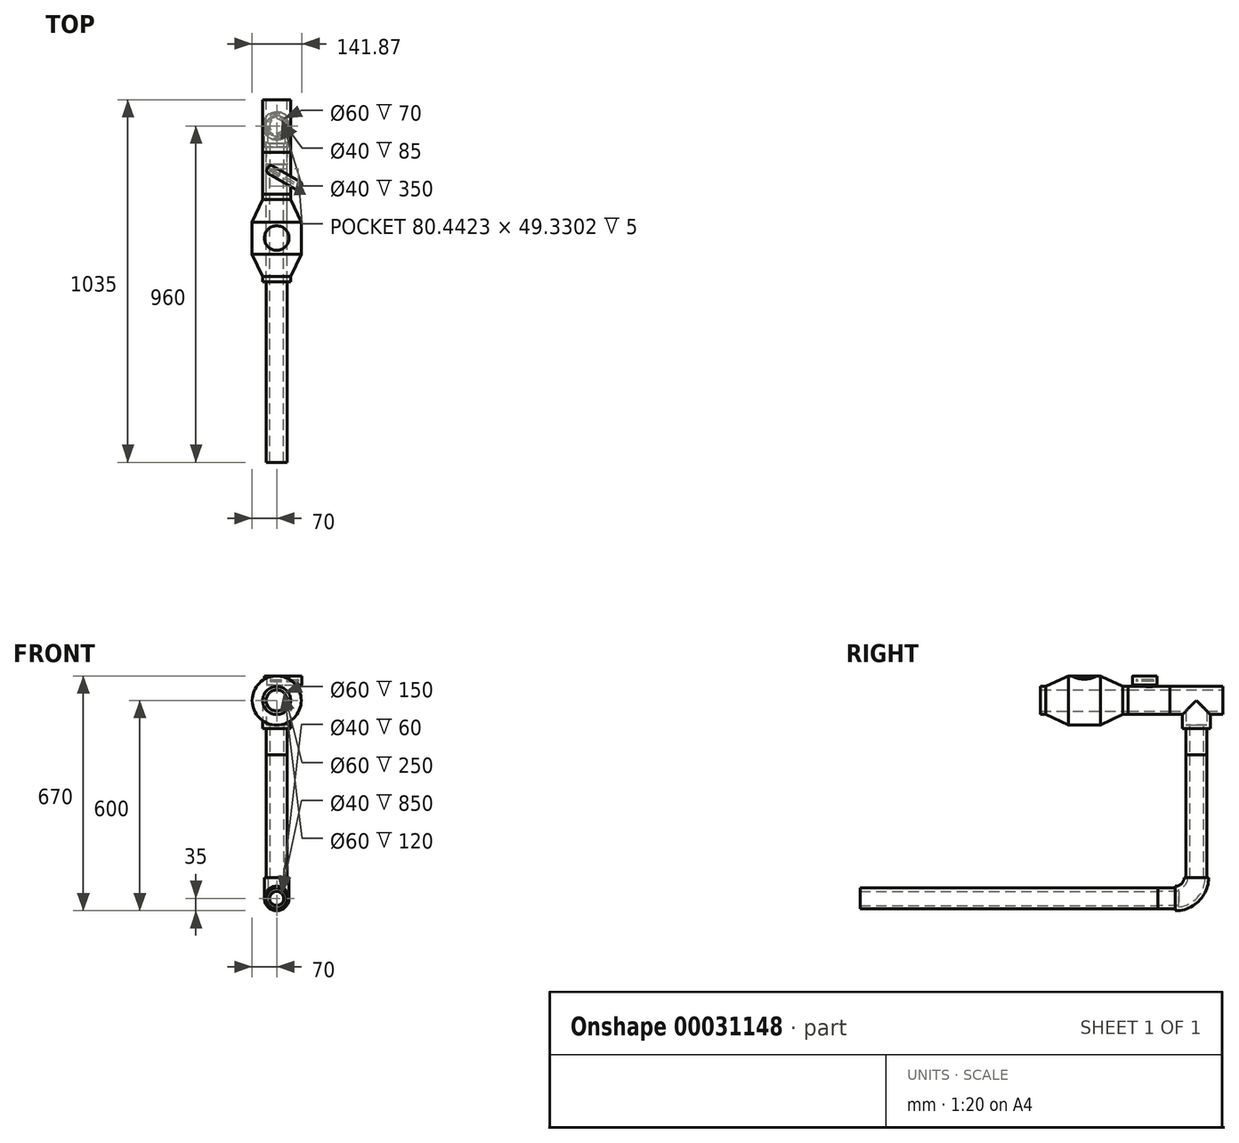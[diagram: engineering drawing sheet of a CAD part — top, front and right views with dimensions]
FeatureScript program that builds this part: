
annotation { "Feature Type Name" : "Feature", "Feature Type Description" : "" }
export const myFeature = defineFeature(function(context is Context, id is Id, definition is map)
    precondition{}
    {
        {
            var Q0;
            Q0=qCreatedBy(makeId("Front.planeOp"),FACE);
            var sketch = newSketch(context, id + "F0", { "sketchPlane" : qUnion([Q0])});
            skCircle(sketch, "E0", {"center": v(0, 0) * mm, "radius": 30 * mm});
            skSolve(sketch);
        }
        {
            var Q0;
            Q0 = qSketchRegion(id + "F0", true);
            extrude(context, id + "F1", {"entities" : qUnion([Q0]), "depth" : 850 * mm});
        }
        {
            var Q0;
            Q0=makeQuery(id+"F1.opExtrude","CAP_FACE",FACE,{"disambiguationData":[OSD([sQuery(id+"F0.wireOp",EDGE,"E0")])],"isStart":true});
            var sketch = newSketch(context, id + "F2", { "sketchPlane" : qUnion([Q0])});
            skCircle(sketch, "E1.0", {"center": v(0, 0) * mm, "radius": 30 * mm});
            skSolve(sketch);
        }
        {
            var Q0;
            Q0 = qSketchRegion(id + "F2", true);
            extrude(context, id + "F3", {"entities" : qUnion([Q0]), "depth" : 50 * mm});
        }
        {
            var Q0;
            Q0=qCreatedBy(makeId("Right.planeOp"),FACE);
            var sketch = newSketch(context, id + "F4", { "sketchPlane" : qUnion([Q0])});
            skArc(sketch, "E2", {"start": v(50, 0) * mm, "mid": v(92.43, 17.57) * mm, "end": v(110, 60) * mm});
            skLineSegment(sketch, "E3", {"start": v(50, 0) * mm, "end": v(-58.8, 0) * mm, "construction": true});
            skLineSegment(sketch, "E4", {"start": v(110, 60) * mm, "end": v(110, 125.75) * mm, "construction": true});
            skSolve(sketch);
        }
        {
            var Q0;
            Q0=makeQuery(id+"F3.opExtrude","CAP_FACE",FACE,{"disambiguationData":[OSD([sQuery(id+"F2.wireOp",EDGE,"E1.0")])],"isStart":false});
            var sketch = newSketch(context, id + "F5", { "sketchPlane" : qUnion([Q0])});
            skCircle(sketch, "E5", {"center": v(0, 0) * mm, "radius": 35 * mm});
            skSolve(sketch);
        }
        {
            var Q0;
            Q0 = qSketchRegion(id + "F5", true);
            var Q1;
            Q1 = qConstructionFilter(qBodyType(qCreatedBy(id + "F4" ,EDGE), BodyType.WIRE), ConstructionObject.NO);
            sweep(context, id + "F6", {"operationType" : NewBodyOperationType.ADD, "profiles" : qUnion([Q0]), "path" : qUnion([Q1])});
        }
        {
            var Q0;
            Q0=makeQuery(id+"F6.opSweep","CAP_FACE",FACE,{"disambiguationData":[OSD([sQuery(id+"F4.wireOp",VERTEX,"E2.end"),sQuery(id+"F5.wireOp",EDGE,"E5")])],"isStart":false});
            var sketch = newSketch(context, id + "F7", { "sketchPlane" : qUnion([Q0])});
            skCircle(sketch, "E6", {"center": v(0, 110) * mm, "radius": 30 * mm});
            skPoint(sketch, "E7", {"position": v(0, 140) * mm});
            skSolve(sketch);
        }
        {
            var Q0;
            Q0 = qSketchRegion(id + "F7", true);
            extrude(context, id + "F8", {"entities" : qUnion([Q0]), "depth" : 350 * mm});
        }
        {
            var Q0;
            Q0=makeQuery(id+"F8.opExtrude","CAP_FACE",FACE,{"disambiguationData":[OSD([sQuery(id+"F7.wireOp",EDGE,"E6")])],"isStart":false});
            var sketch = newSketch(context, id + "F9", { "sketchPlane" : qUnion([Q0])});
            skCircle(sketch, "E8.0", {"center": v(0, 110) * mm, "radius": 30 * mm});
            skSolve(sketch);
        }
        {
            var Q0;
            Q0 = qSketchRegion(id + "F9", true);
            extrude(context, id + "F10", {"entities" : qUnion([Q0]), "depth" : 75 * mm});
        }
        {
            var Q0;
            Q0=makeQuery(id+"F10.opExtrude","CAP_FACE",FACE,{"disambiguationData":[OSD([sQuery(id+"F9.wireOp",EDGE,"E8.0")])],"isStart":false});
            var sketch = newSketch(context, id + "F11", { "sketchPlane" : qUnion([Q0])});
            skCircle(sketch, "E9", {"center": v(0, 110) * mm, "radius": 40 * mm});
            skSolve(sketch);
        }
        {
            var Q0;
            Q0 = qSketchRegion(id + "F11", true);
            extrude(context, id + "F12", {"entities" : qUnion([Q0]), "operationType" : NewBodyOperationType.ADD, "depth" : 80 * mm});
        }
        {
            var Q0;
            Q0=sQuery(id+"F11.wireOp",VERTEX,"E9.center");
            var Q1;
            Q1=qCreatedBy(makeId("Front.planeOp"),FACE);
            cPlane(context, id + "F13", {"entities" : qUnion([Q0, Q1]), "cplaneType" : CPlaneType.PLANE_POINT, "offset" : 150 * mm, "width" : 150 * mm, "height" : 150 * mm});
        }
        {
            var Q0;
            Q0=qCreatedBy(id+"F13.planeOp",FACE);
            var sketch = newSketch(context, id + "F14", { "sketchPlane" : qUnion([Q0])});
            skCircle(sketch, "E10", {"center": v(0, 565) * mm, "radius": 40 * mm});
            skSolve(sketch);
        }
        {
            var Q0;
            Q0 = qSketchRegion(id + "F14", true);
            extrude(context, id + "F15", {"entities" : qUnion([Q0]), "operationType" : NewBodyOperationType.ADD, "depth" : 150 * mm, "symmetric" : true});
        }
        {
            var Q0;
            Q0=makeQuery(id+"F15.opExtrude","CAP_FACE",FACE,{"disambiguationData":[OSD([sQuery(id+"F14.wireOp",EDGE,"E10")])],"isStart":false});
            var sketch = newSketch(context, id + "F16", { "sketchPlane" : qUnion([Q0])});
            skCircle(sketch, "E11.0", {"center": v(0, 565) * mm, "radius": 40 * mm});
            skSolve(sketch);
        }
        {
            var Q0;
            Q0 = qSketchRegion(id + "F16", true);
            extrude(context, id + "F17", {"entities" : qUnion([Q0]), "depth" : 120 * mm});
        }
        {
            var Q0;
            Q0=qCreatedBy(makeId("Right.planeOp"),FACE);
            var sketch = newSketch(context, id + "F18", { "sketchPlane" : qUnion([Q0])});
            skLineSegment(sketch, "E12", {"start": v(-25, 565) * mm, "end": v(-25, 610) * mm});
            skLineSegment(sketch, "E13", {"start": v(-25, 565) * mm, "end": v(-35, 565) * mm});
            skLineSegment(sketch, "E14", {"start": v(-35, 565) * mm, "end": v(-35, 610) * mm});
            skLineSegment(sketch, "E15", {"start": v(-35, 610) * mm, "end": v(-25, 610) * mm});
            skSolve(sketch);
        }
        {
            var Q0;
            Q0 = qSketchRegion(id + "F18", true);
            var Q1;
            Q1=sQuery(id+"F18.wireOp",EDGE,"E12");
            revolve(context, id + "F19", {"operationType" : NewBodyOperationType.ADD, "entities" : qUnion([Q0]), "axis" : qUnion([Q1]), "revolveType" : RevolveType.FULL});
        }
        {
            var Q0;
            Q0=makeQuery(id+"F19.opRevolve","SWEPT_FACE",FACE,{"disambiguationData":[OSD([sQuery(id+"F18.wireOp",EDGE,"E15")])]});
            var sketch = newSketch(context, id + "F20", { "sketchPlane" : qUnion([Q0])});
            skLineSegment(sketch, "E16.bottom", {"start": v(-11.07, -4.17) * mm, "end": v(66.87, -49.17) * mm});
            skLineSegment(sketch, "E16.top", {"start": v(-23.57, -25.83) * mm, "end": v(54.37, -70.83) * mm});
            skLineSegment(sketch, "E16.left", {"start": v(-24.73, -7.83) * mm, "end": v(-27.23, -12.17) * mm});
            skLineSegment(sketch, "E16.right", {"start": v(70.53, -62.83) * mm, "end": v(68.03, -67.17) * mm});
            skLineSegment(sketch, "E17", {"start": v(-25.98, -10) * mm, "end": v(69.28, -65) * mm, "construction": true});
            skPoint(sketch, "E18", {"position": v(0, -25) * mm});
            skPoint(sketch, "E19.visualSharp", {"position": v(-19.73, 0.83) * mm});
            skArc(sketch, "E19.filletArc", {"start": v(-11.07, -4.17) * mm, "mid": v(-18.66, -3.18) * mm, "end": v(-24.73, -7.83) * mm});
            skPoint(sketch, "E20.visualSharp", {"position": v(75.53, -54.17) * mm});
            skArc(sketch, "E20.filletArc", {"start": v(70.53, -62.83) * mm, "mid": v(71.53, -55.25) * mm, "end": v(66.87, -49.17) * mm});
            skPoint(sketch, "E21.visualSharp", {"position": v(63.03, -75.83) * mm});
            skArc(sketch, "E21.filletArc", {"start": v(54.37, -70.83) * mm, "mid": v(61.96, -71.82) * mm, "end": v(68.03, -67.17) * mm});
            skPoint(sketch, "E22.visualSharp", {"position": v(-32.23, -20.83) * mm});
            skArc(sketch, "E22.filletArc", {"start": v(-27.23, -12.17) * mm, "mid": v(-28.23, -19.75) * mm, "end": v(-23.57, -25.83) * mm});
            skLineSegment(sketch, "E23", {"start": v(0, -25) * mm, "end": v(80.42, -25) * mm, "construction": true});
            skSolve(sketch);
        }
        {
            var Q0;
            Q0 = qSketchRegion(id + "F20", true);
            extrude(context, id + "F21", {"entities" : qUnion([Q0]), "operationType" : NewBodyOperationType.ADD, "depth" : 25 * mm});
        }
        {
            var Q0;
            Q0=makeQuery(id+"F17.opExtrude","CAP_FACE",FACE,{"disambiguationData":[OSD([sQuery(id+"F16.wireOp",EDGE,"E11.0")])],"isStart":false});
            var sketch = newSketch(context, id + "F22", { "sketchPlane" : qUnion([Q0])});
            skCircle(sketch, "E24.0", {"center": v(0, 565) * mm, "radius": 40 * mm});
            skSolve(sketch);
        }
        {
            var Q0;
            Q0 = qSketchRegion(id + "F22", true);
            extrude(context, id + "F23", {"entities" : qUnion([Q0]), "depth" : 250 * mm});
        }
        {
            var Q0;
            Q0=makeQuery(id+"F17.opExtrude","CAP_FACE",FACE,{"disambiguationData":[OSD([sQuery(id+"F16.wireOp",EDGE,"E11.0")])],"isStart":false});
            var Q1;
            Q1=makeQuery(id+"F15.opExtrude","CAP_FACE",FACE,{"disambiguationData":[OSD([sQuery(id+"F14.wireOp",EDGE,"E10")])],"isStart":true});
            var Q2;
            Q2=makeQuery(id+"F1.opExtrude","CAP_FACE",FACE,{"disambiguationData":[OSD([sQuery(id+"F0.wireOp",EDGE,"E0")])],"isStart":false});
            var Q3;
            Q3=makeQuery(id+"F3.opExtrude","CAP_FACE",FACE,{"disambiguationData":[OSD([sQuery(id+"F2.wireOp",EDGE,"E1.0")])],"isStart":true});
            var Q4;
            Q4=makeQuery(id+"F6.opSweep","CAP_FACE",FACE,{"disambiguationData":[OSD([sQuery(id+"F4.wireOp",VERTEX,"E2.end"),sQuery(id+"F5.wireOp",EDGE,"E5")])],"isStart":false});
            var Q5;
            Q5=makeQuery(id+"F10.opExtrude","CAP_FACE",FACE,{"disambiguationData":[OSD([sQuery(id+"F9.wireOp",EDGE,"E8.0")])],"isStart":true});
            var Q6;
            Q6=makeQuery(id+"F15.opExtrude","CAP_FACE",FACE,{"disambiguationData":[OSD([sQuery(id+"F14.wireOp",EDGE,"E10")])],"isStart":false});
            var Q7;
            Q7=makeQuery(id+"F8.opExtrude","CAP_FACE",FACE,{"disambiguationData":[OSD([sQuery(id+"F7.wireOp",EDGE,"E6")])],"isStart":false});
            var Q8;
            Q8=makeQuery(id+"F17.opExtrude","CAP_FACE",FACE,{"disambiguationData":[OSD([sQuery(id+"F16.wireOp",EDGE,"E11.0")])],"isStart":true});
            var Q9;
            Q9=makeQuery(id+"F8.opExtrude","CAP_FACE",FACE,{"disambiguationData":[OSD([sQuery(id+"F7.wireOp",EDGE,"E6")])],"isStart":true});
            var Q10;
            Q10=makeQuery(id+"F1.opExtrude","CAP_FACE",FACE,{"disambiguationData":[OSD([sQuery(id+"F0.wireOp",EDGE,"E0")])],"isStart":true});
            var Q11;
            Q11=makeQuery(id+"F23.opExtrude","CAP_FACE",FACE,{"disambiguationData":[OSD([sQuery(id+"F22.wireOp",EDGE,"E24.0")])],"isStart":false});
            var Q12;
            Q12=makeQuery(id+"F23.opExtrude","CAP_FACE",FACE,{"disambiguationData":[OSD([sQuery(id+"F22.wireOp",EDGE,"E24.0")])],"isStart":true});
            var Q13;
            Q13=makeQuery(id+"F17.opExtrude","SWEPT_BODY",BODY,{"disambiguationData":[OSD([sQuery(id+"F16.wireOp",EDGE,"E11.0")])]});
            var Q14;
            Q14=makeQuery(id+"F8.opExtrude","SWEPT_BODY",BODY,{"disambiguationData":[OSD([sQuery(id+"F7.wireOp",EDGE,"E6")])]});
            var Q15;
            Q15=makeQuery(id+"F10.opExtrude","SWEPT_BODY",BODY,{"disambiguationData":[OSD([sQuery(id+"F9.wireOp",EDGE,"E8.0")])]});
            var Q16;
            Q16=makeQuery(id+"F3.opExtrude","SWEPT_BODY",BODY,{"disambiguationData":[OSD([sQuery(id+"F2.wireOp",EDGE,"E1.0")])]});
            var Q17;
            Q17=makeQuery(id+"F1.opExtrude","SWEPT_BODY",BODY,{"disambiguationData":[OSD([sQuery(id+"F0.wireOp",EDGE,"E0")])]});
            shell(context, id + "F24", {"entities" : qUnion([Q0, Q1, Q2, Q3, Q4, Q5, Q6, Q7, Q8, Q9, Q10, Q11, Q12]), "parts" : qUnion([Q13, Q14, Q15, Q16, Q17]), "thickness" : 10 * mm});
        }
        {
            var Q0;
            Q0=qCreatedBy(makeId("Right.planeOp"),FACE);
            var sketch = newSketch(context, id + "F25", { "sketchPlane" : qUnion([Q0])});
            skLineSegment(sketch, "E25", {"start": v(-100, 605) * mm, "end": v(-320, 605) * mm});
            skLineSegment(sketch, "E26", {"start": v(-320, 605) * mm, "end": v(-255.66, 635) * mm});
            skLineSegment(sketch, "E27", {"start": v(-255.66, 635) * mm, "end": v(-164.34, 635) * mm});
            skLineSegment(sketch, "E28", {"start": v(-100, 605) * mm, "end": v(-164.34, 635) * mm});
            skLineSegment(sketch, "E29", {"start": v(-210, 635) * mm, "end": v(-210, 514.36) * mm, "construction": true});
            skLineSegment(sketch, "E30", {"start": v(-123, 565) * mm, "end": v(-324.22, 565) * mm, "construction": true});
            skSolve(sketch);
        }
        {
            var Q0;
            Q0 = qSketchRegion(id + "F25", true);
            var Q1;
            Q1=sQuery(id+"F25.wireOp",EDGE,"E30");
            revolve(context, id + "F26", {"operationType" : NewBodyOperationType.ADD, "entities" : qUnion([Q0]), "axis" : qUnion([Q1]), "revolveType" : RevolveType.FULL});
        }
        {
            var Q0;
            Q0=qCreatedBy(makeId("Right.planeOp"),FACE);
            var sketch = newSketch(context, id + "F27", { "sketchPlane" : qUnion([Q0])});
            skLineSegment(sketch, "E31.bottom", {"start": v(-175, 635) * mm, "end": v(-210, 635) * mm});
            skLineSegment(sketch, "E31.top", {"start": v(-175, 605) * mm, "end": v(-210, 605) * mm});
            skLineSegment(sketch, "E31.left", {"start": v(-175, 635) * mm, "end": v(-175, 605) * mm});
            skLineSegment(sketch, "E31.right", {"start": v(-210, 635) * mm, "end": v(-210, 605) * mm});
            skSolve(sketch);
        }
        {
            var Q0;
            Q0 = qSketchRegion(id + "F27", true);
            var Q1;
            Q1=sQuery(id+"F27.wireOp",EDGE,"E31.right");
            revolve(context, id + "F28", {"operationType" : NewBodyOperationType.ADD, "entities" : qUnion([Q0]), "axis" : qUnion([Q1]), "revolveType" : RevolveType.FULL});
        }
    });
